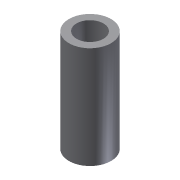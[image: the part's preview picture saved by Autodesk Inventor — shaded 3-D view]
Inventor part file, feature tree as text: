
AUTODESK INVENTOR PART (.ipt)
format: ipt  version: 2012 (Build 160160000, 160)  size: 72,704 bytes
history: native  units: mm
features: extrude x1, sketch x1
ambient origin geometry x8: Origin, YZ Plane, XZ Plane, XY Plane, X Axis, Y Axis, Z Axis, Center Point
bodies: Solid1 (feature_tree)
feature tree (2):
  extrude  "Extrusion1"  Depth=5.1mm
  sketch  "Sketch1"  dims[d0=8.0mm d1=5.1mm d2=19.4mm d3=0.0mm]
